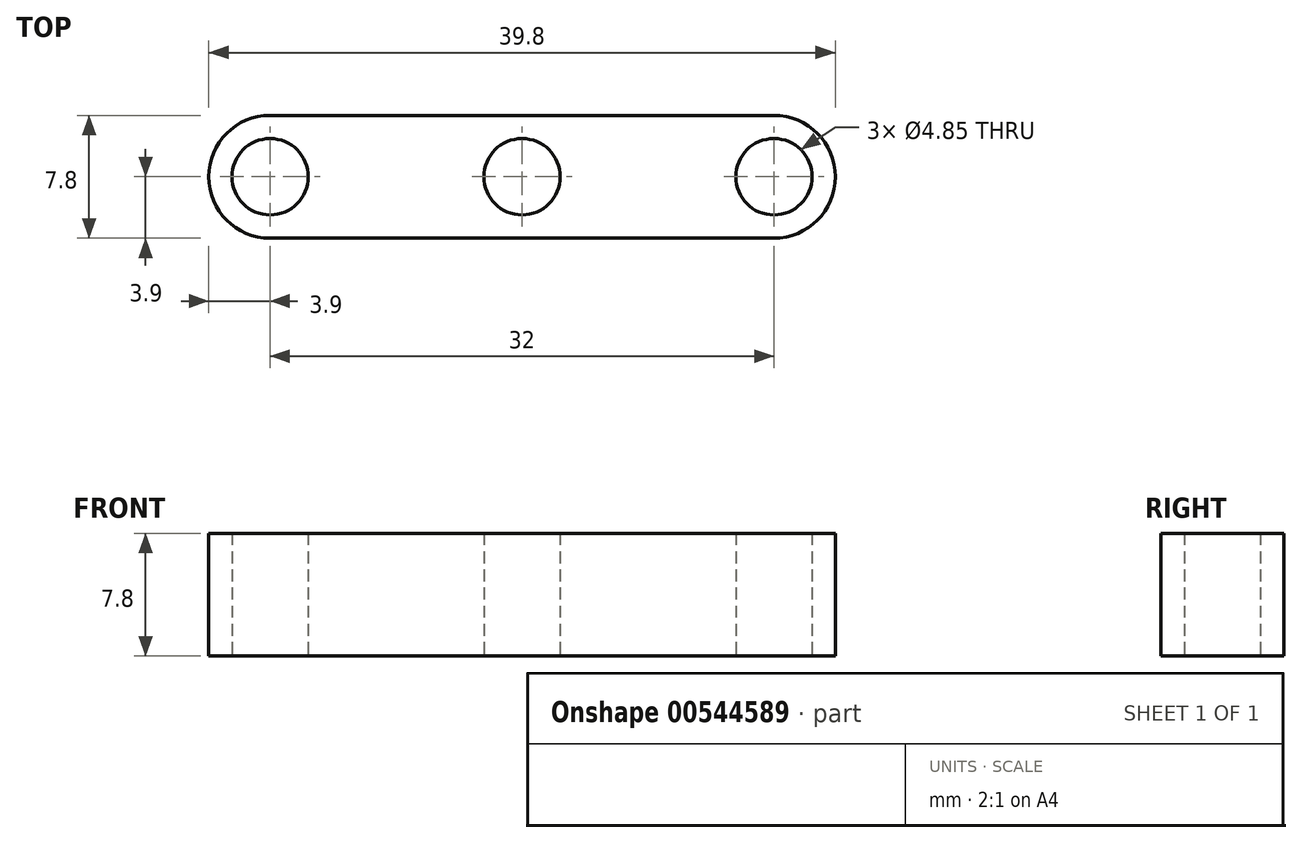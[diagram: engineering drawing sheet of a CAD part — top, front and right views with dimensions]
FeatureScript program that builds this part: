
annotation { "Feature Type Name" : "Feature", "Feature Type Description" : "" }
export const myFeature = defineFeature(function(context is Context, id is Id, definition is map)
    precondition{}
    {
        {
            var Q0;
            Q0=qCreatedBy(makeId("Top.planeOp"),FACE);
            var sketch = newSketch(context, id + "F0", { "sketchPlane" : qUnion([Q0])});
            skLineSegment(sketch, "E0.bottom", {"start": v(16, 3.9) * mm, "end": v(-16, 3.9) * mm});
            skLineSegment(sketch, "E0.top", {"start": v(16, -3.9) * mm, "end": v(-16, -3.9) * mm});
            skPoint(sketch, "E0.middle", {"position": v(0, 0) * mm});
            skArc(sketch, "E1", {"start": v(16, -3.9) * mm, "mid": v(19.9, 0) * mm, "end": v(16, 3.9) * mm});
            skArc(sketch, "E2", {"start": v(-16, 3.9) * mm, "mid": v(-19.9, 0) * mm, "end": v(-16, -3.9) * mm});
            skCircle(sketch, "E3", {"center": v(0, 0) * mm, "radius": 2.43 * mm});
            skCircle(sketch, "E4", {"center": v(16, 0) * mm, "radius": 2.43 * mm});
            skCircle(sketch, "E5", {"center": v(-16, 0) * mm, "radius": 2.43 * mm});
            skSolve(sketch);
        }
        {
            var Q0;
            Q0=makeQuery(id+"F0.imprint","IMPRINT",FACE,{"disambiguationData":[TD([[makeQuery(id+"F0.imprint","IMPRINT",EDGE,{"derivedFrom":sQuery(id+"F0.wireOp",EDGE,"E0.bottom")}),1.0]])]});
            extrude(context, id + "F1", {"entities" : qUnion([Q0]), "depth" : 7.8 * mm, "offsetDistance" : 25 * mm});
        }
        {
            var Q0;
            Q0=makeQuery(id+"F1.opExtrude","SWEPT_FACE",FACE,{"disambiguationData":[OSD([sQuery(id+"F0.wireOp",EDGE,"E0.top")])]});
            var sketch = newSketch(context, id + "F2", { "sketchPlane" : qUnion([Q0])});
            skLineSegment(sketch, "E6", {"start": v(0, 0) * mm, "end": v(0, 3.9) * mm});
            skPoint(sketch, "E6.endSnap0", {"position": v(0, 0) * mm});
            skLineSegment(sketch, "E7", {"start": v(0, 3.9) * mm, "end": v(8, 3.9) * mm});
            skLineSegment(sketch, "E8", {"start": v(0, 3.9) * mm, "end": v(-8, 3.9) * mm});
            skCircle(sketch, "E9", {"center": v(8, 3.9) * mm, "radius": 2.43 * mm});
            skCircle(sketch, "E10", {"center": v(-8, 3.9) * mm, "radius": 2.43 * mm});
            skSolve(sketch);
        }
        {
            var Q0;
            Q0=makeQuery(id+"F2.imprint","IMPRINT",FACE,{"disambiguationData":[TD([[makeQuery(id+"F2.imprint","IMPRINT",EDGE,{"derivedFrom":sQuery(id+"F2.wireOp",EDGE,"E10")}),1.0]])]});
            var Q1;
            Q1=makeQuery(id+"F2.imprint","IMPRINT",FACE,{"disambiguationData":[TD([[makeQuery(id+"F2.imprint","IMPRINT",EDGE,{"derivedFrom":sQuery(id+"F2.wireOp",EDGE,"E9")}),1.0]])]});
            extrude(context, id + "F3", {"entities" : qUnion([Q0, Q1]), "operationType" : NewBodyOperationType.ADD, "depth" : -7.8 * mm, "offsetDistance" : 25 * mm});
        }
    });
